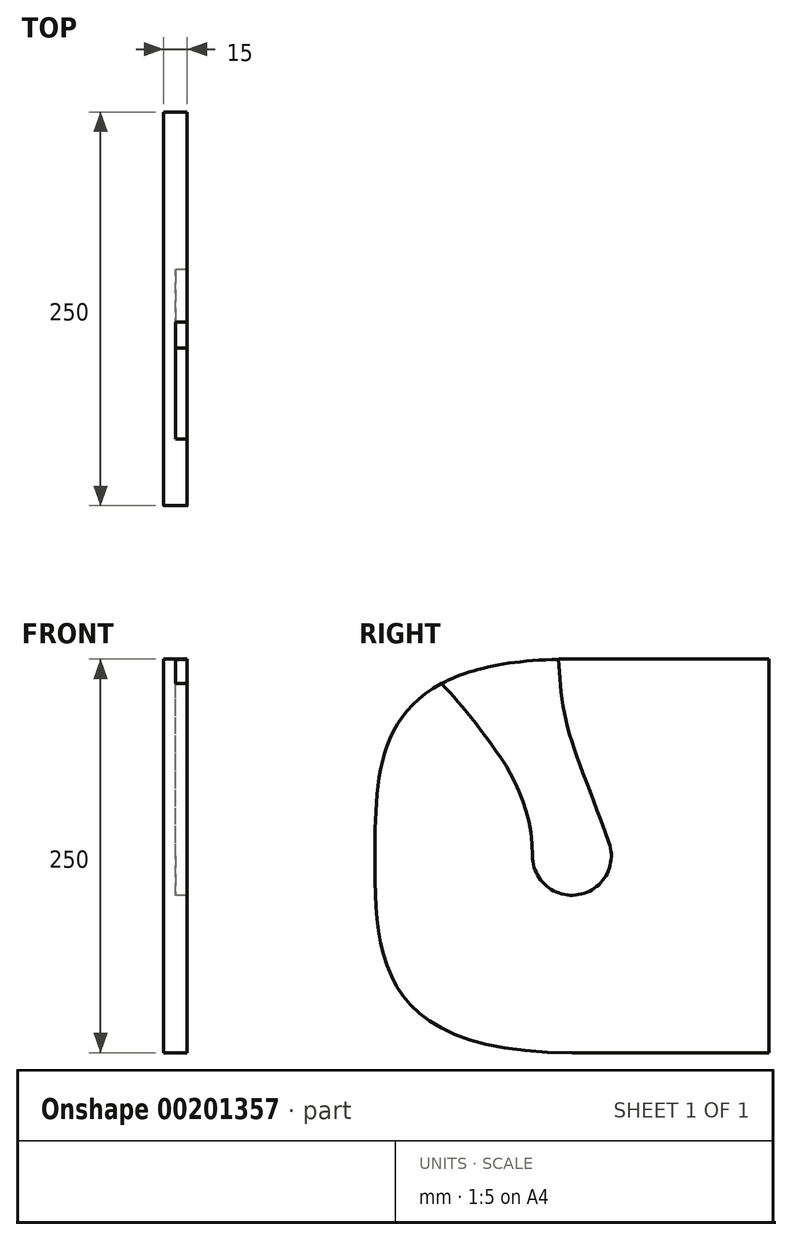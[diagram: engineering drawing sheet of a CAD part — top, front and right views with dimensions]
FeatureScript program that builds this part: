
annotation { "Feature Type Name" : "Feature", "Feature Type Description" : "" }
export const myFeature = defineFeature(function(context is Context, id is Id, definition is map)
    precondition{}
    {
        {
            assignVariable(context, id + "F0", {"name" : "Thickness", "anyValue" : 15});
        }
        {
            var Q0;
            Q0=qCreatedBy(makeId("Right.planeOp"),FACE);
            var sketch = newSketch(context, id + "F1", { "sketchPlane" : qUnion([Q0])});
            skLineSegment(sketch, "E0.bottom", {"start": v(0, -125) * mm, "end": v(-250, -125) * mm});
            skLineSegment(sketch, "E0.top", {"start": v(0, 125) * mm, "end": v(-250, 125) * mm});
            skLineSegment(sketch, "E0.left", {"start": v(0, -125) * mm, "end": v(0, 125) * mm});
            skLineSegment(sketch, "E0.right", {"start": v(-250, -125) * mm, "end": v(-250, 125) * mm});
            skLineSegment(sketch, "E1", {"start": v(159.42, 0) * mm, "end": v(-365.23, 0) * mm, "construction": true});
            skFitSpline(sketch, "E2", {"points": [v(-125, 125) * mm, v(-250, 0) * mm, v(-125, -125) * mm], "startDerivative": vector(-750, 0) * mm, "endDerivative": vector(750, 0) * mm});
            skCircle(sketch, "E3", {"center": v(-125, 0) * mm, "radius": 25 * mm});
            skFitSpline(sketch, "E4", {"points": [v(-150, 0) * mm, v(-181.69, 78.4) * mm, v(-207.83, 109.44) * mm], "startDerivative": vector(0, 177.9) * mm, "endDerivative": vector(-61.05, 61.92) * mm});
            skFitSpline(sketch, "E5", {"points": [v(-101.43, 8.33) * mm, v(-128.14, 83.38) * mm, v(-133.42, 124.9) * mm], "startDerivative": vector(-60.4, 170.85) * mm, "endDerivative": vector(-3.48, 92.83) * mm});
            skSolve(sketch);
        }
        {
            var Q0;
            {var subQ4=sQuery(id+"F1.wireOp",EDGE,"E0.left");Q0=makeQuery(id+"F1.imprint","IMPRINT",FACE,{"disambiguationData":[TD([[makeQuery(id+"F1.imprint","IMPRINT",EDGE,{"derivedFrom":subQ4}),1.0]])]});}
            extrude(context, id + "F2", {"entities" : qUnion([Q0]), "depth" : (getVariable(context, 'Thickness') / 2) * mm});
        }
        {
            var Q0;
            {var subQ4=sQuery(id+"F1.wireOp",EDGE,"E0.left");Q0=makeQuery(id+"F1.imprint","IMPRINT",FACE,{"disambiguationData":[TD([[makeQuery(id+"F1.imprint","IMPRINT",EDGE,{"derivedFrom":subQ4}),1.0]])]});}
            var Q1;
            {var subQ0=sQuery(id+"F1.wireOp",EDGE,"E4");Q1=makeQuery(id+"F1.imprint","IMPRINT",FACE,{"disambiguationData":[TD([[makeQuery(id+"F1.imprint","IMPRINT",EDGE,{"derivedFrom":subQ0}),-1.0]])]});}
            var Q2;
            {var subQ0=sQuery(id+"F1.wireOp",EDGE,"E3");var subQ1=makeQuery(id+"F1.imprint","INTERSECT",VERTEX,{"derivedFrom":[subQ0,sQuery(id+"F1.wireOp",EDGE,"E4")]});Q2=makeQuery(id+"F1.imprint","IMPRINT",FACE,{"disambiguationData":[TD([[makeQuery(id+"F1.imprint","IMPRINT",EDGE,{"disambiguationData":[TD([[subQ1,1.0]])],"derivedFrom":subQ0}),1.0]])]});}
            extrude(context, id + "F3", {"entities" : qUnion([Q0, Q1, Q2]), "operationType" : NewBodyOperationType.ADD, "oppositeDirection" : true, "depth" : (getVariable(context, 'Thickness') / 2) * mm});
        }
    });
